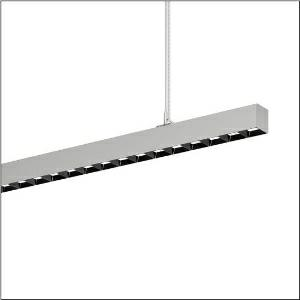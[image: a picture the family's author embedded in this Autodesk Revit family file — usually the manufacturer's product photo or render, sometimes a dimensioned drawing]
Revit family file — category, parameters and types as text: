
# Revit family: silica_21_51mx31dc3dsb
name_source: partatom
category: Lighting Fixtures
units: mm (PartAtom-declared; Revit-internal decimal feet)

## family parameters
Cut with Voids When Loaded = No
Host = Face
Light Source = No
Part Type = Normal
Room Calculation Point = No
Round Connector Dimension = Use Diameter
Shared = No

## types (1)
- --- (1 x LED, 18230 lm, 113.3 W, 3000K)
    Apparent Load = 113 VA
    CIE Flux Codes = 87 99 100 59 100
    Color Rendering = 80
    Color Temperature = 3000K
    Default Elevation = 1800 mm
    Description = Silica 21, office luminaire, primary light control with darklight reflector, of PMMA, black, CAT 2 (L<= 3000cd/m²), light emission: direct/indirect distribution, primary light characteristic: symmetric, installation type: suspended mounting, LED, rated luminous flux: 18.230lm, luminous efficacy: 161lm/W, light colour: 830, colour temperature: 3000K, control gear: DALI 2, with terminal, 3+2-pole, max. 2.5mm², mains connection: 220..240V, AC, 50/60Hz, rated input power: 113.3W, luminaire housing, of aluminium, metallic grey (RAL 9006), length: 3.004mm, width: 53mm, height: 53mm, protection rating (complete): IP20, insulation class (complete): insulation class I (protective earthing), certification: CE, permissible operating ambient temperature: 0..+35°C, standard: EN 50419, packaging unit: 1 piece
    Height = 53 mm
    Lamp = 1 x LED
    Lamp Light Flux = 18230 lm
    Lamp Power = 113.3 W
    Lamp count = 1
    Length = 3004 mm
    Luminous efficacy = 161 lm/W
    Manufacturer = Siteco
    ModVariant = No
    Model = 51MX31DC3DSB
    Mounting Place = Ceiling
    Mounting Type = Pendant
    Number of Poles = 1
    OnlyDefault = Yes
    Power Factor = 1
    Product Name = Silica 21
    Product group = office luminaire | ceiling pendant
    ProductGroupID = 903
    Protection Class = Protection class I
    Protection Degree = IP 20
    RLX_Detail_Level = 1
    RLX_Emergency_Light_Flux = 0 lm
    RLX_Emergency_Type = 0
    RLX_Emergency_Type_DB = No
    RlxData = <blob elided: 65449 chars, md5=a58280cf>
    Socket = socket
    Standby Power = 0 W
    System Light Flux = 18230 lm
    System Power = 113 W
    Type Comments = factory setting: luminous flux: 100 % | dim-lin: 254 | 392 mA
    Type Image = l_1335859.jpg
    URL = http://relux.com
    VarID = @adj_121101
    Voltage = 0 V
    Weight = 0.00 kg
    Width = 53 mm

## geometry (parser evidence)
native form markers: Blend x4, Sweep x12
no freeform markers — native parametric forms only
